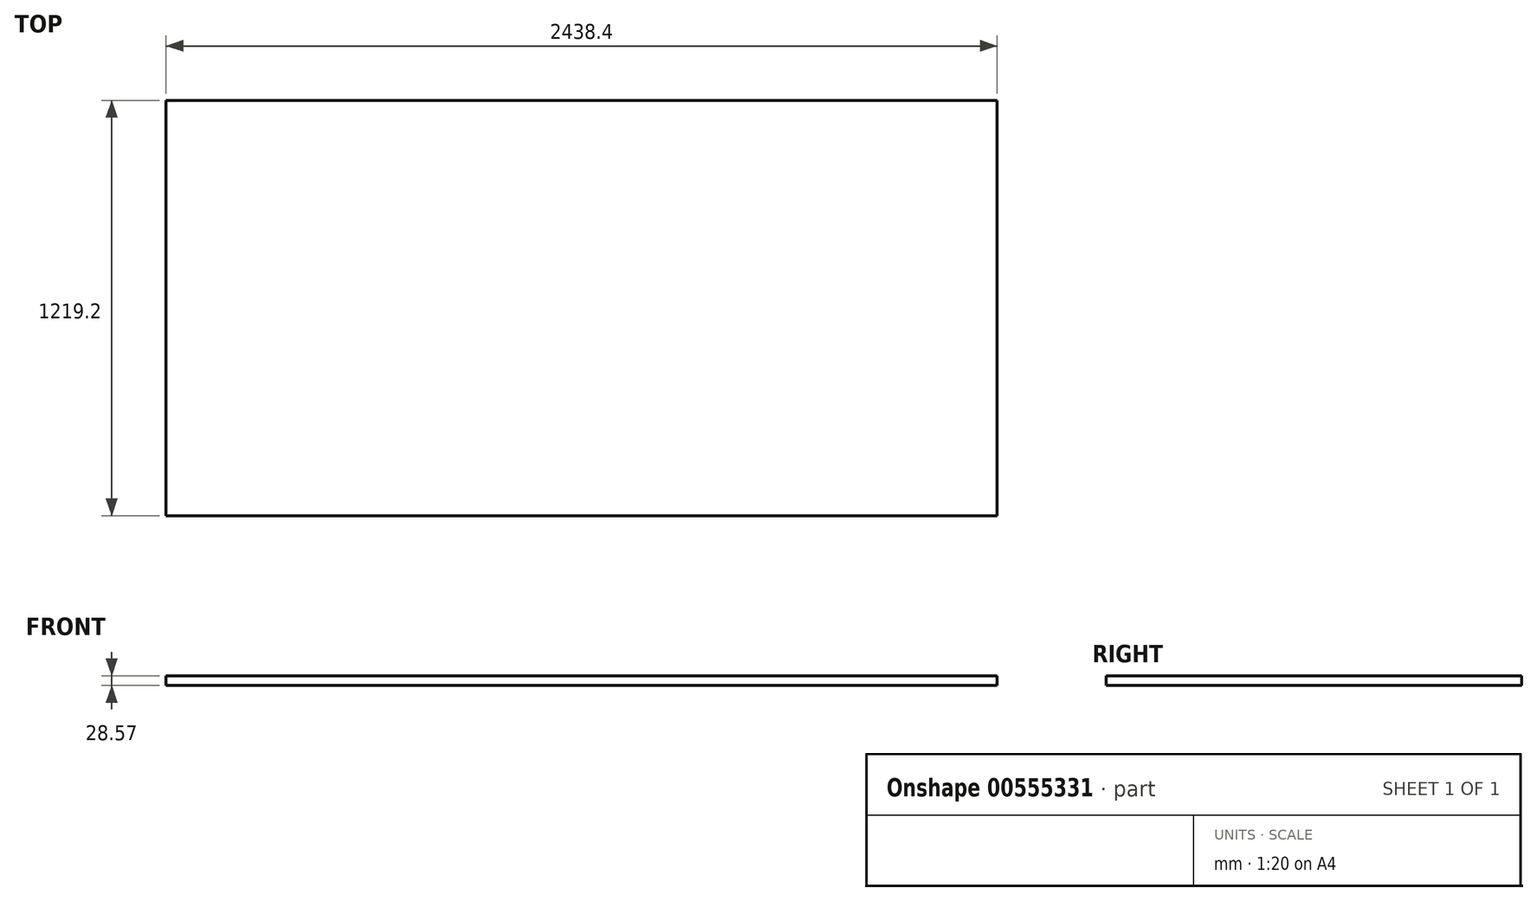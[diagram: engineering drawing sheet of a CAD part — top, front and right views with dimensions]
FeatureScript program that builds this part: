
annotation { "Feature Type Name" : "Feature", "Feature Type Description" : "" }
export const myFeature = defineFeature(function(context is Context, id is Id, definition is map)
    precondition{}
    {
        {
            var Q0;
            Q0=qCreatedBy(makeId("Top.planeOp"),FACE);
            var sketch = newSketch(context, id + "F0", { "sketchPlane" : qUnion([Q0])});
            skLineSegment(sketch, "E0.bottom", {"start": v(1219.2, 609.6) * mm, "end": v(-1219.2, 609.6) * mm});
            skLineSegment(sketch, "E0.top", {"start": v(1219.2, -609.6) * mm, "end": v(-1219.2, -609.6) * mm});
            skLineSegment(sketch, "E0.left", {"start": v(1219.2, 609.6) * mm, "end": v(1219.2, -609.6) * mm});
            skLineSegment(sketch, "E0.right", {"start": v(-1219.2, 609.6) * mm, "end": v(-1219.2, -609.6) * mm});
            skPoint(sketch, "E0.middle", {"position": v(0, 0) * mm});
            skSolve(sketch);
        }
        {
            var Q0;
            Q0=makeQuery(id+"F0.imprint","IMPRINT",FACE,{"disambiguationData":[TD([[makeQuery(id+"F0.imprint","IMPRINT",EDGE,{"derivedFrom":sQuery(id+"F0.wireOp",EDGE,"E0.bottom")}),1.0]])]});
            extrude(context, id + "F1", {"entities" : qUnion([Q0]), "depth" : 28.57 * mm, "offsetDistance" : 25.4 * mm});
        }
    });
